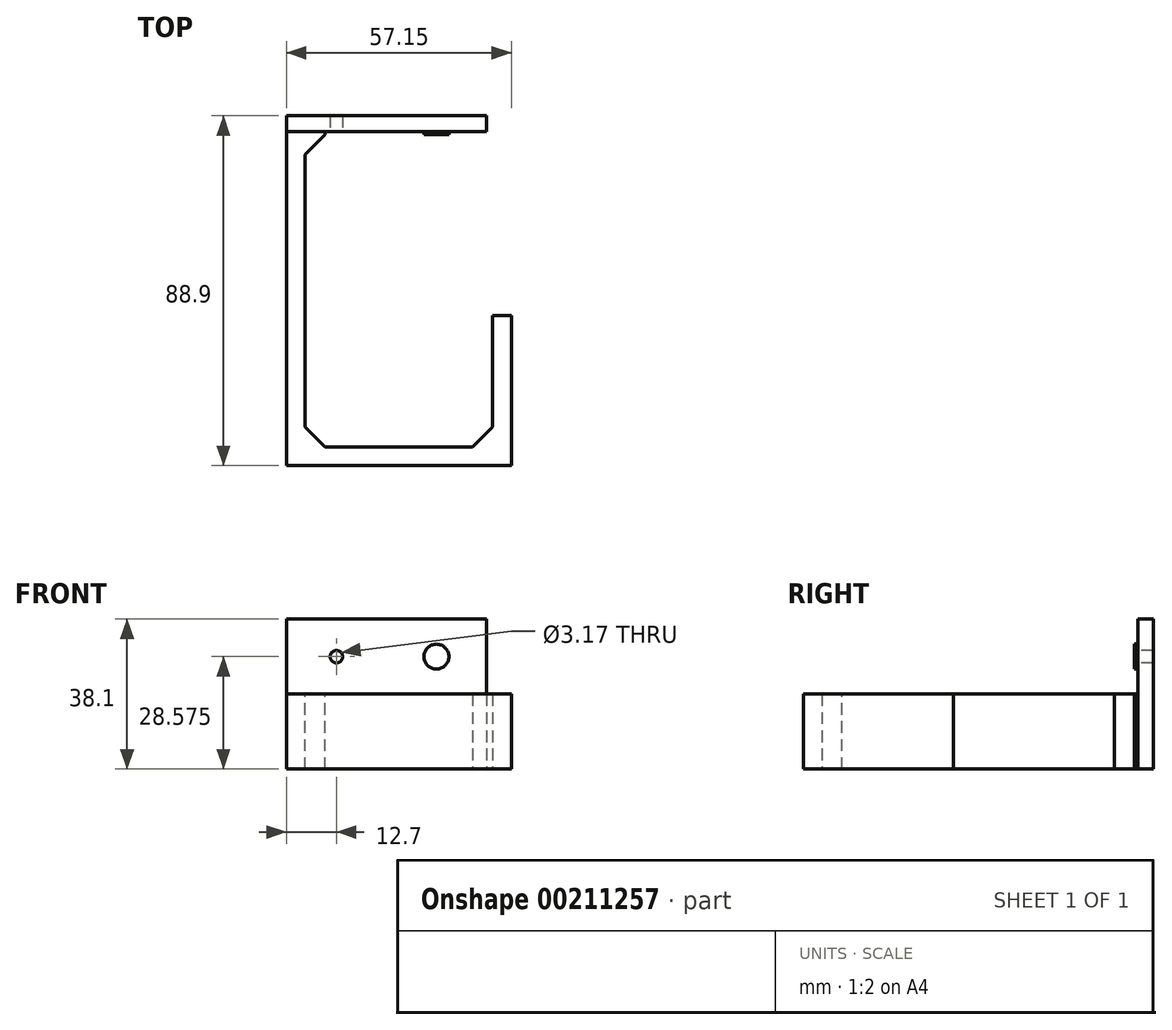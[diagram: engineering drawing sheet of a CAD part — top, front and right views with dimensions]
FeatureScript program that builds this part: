
annotation { "Feature Type Name" : "Feature", "Feature Type Description" : "" }
export const myFeature = defineFeature(function(context is Context, id is Id, definition is map)
    precondition{}
    {
        {
            var Q0;
            Q0=qCreatedBy(makeId("Top.planeOp"),FACE);
            var sketch = newSketch(context, id + "F0", { "sketchPlane" : qUnion([Q0])});
            skLineSegment(sketch, "E0.bottom", {"start": v(-25.4, 25.4) * mm, "end": v(25.4, 25.4) * mm});
            skLineSegment(sketch, "E0.top", {"start": v(-25.4, 30.16) * mm, "end": v(25.4, 30.16) * mm});
            skLineSegment(sketch, "E0.left", {"start": v(-25.4, 25.4) * mm, "end": v(-25.4, 30.16) * mm});
            skLineSegment(sketch, "E0.right", {"start": v(25.4, 25.4) * mm, "end": v(25.4, 30.16) * mm});
            skPoint(sketch, "E0.middle", {"position": v(0, 27.78) * mm});
            skLineSegment(sketch, "E1.bottom", {"start": v(-25.4, 25.4) * mm, "end": v(-20.64, 25.4) * mm});
            skLineSegment(sketch, "E1.top", {"start": v(-25.4, -58.74) * mm, "end": v(-20.64, -58.74) * mm});
            skLineSegment(sketch, "E1.left", {"start": v(-25.4, 25.4) * mm, "end": v(-25.4, -58.74) * mm});
            skLineSegment(sketch, "E1.right", {"start": v(-20.64, 25.4) * mm, "end": v(-20.64, -58.74) * mm});
            skLineSegment(sketch, "E2.bottom", {"start": v(-20.64, -58.74) * mm, "end": v(31.75, -58.74) * mm});
            skLineSegment(sketch, "E2.top", {"start": v(-20.64, -53.98) * mm, "end": v(31.75, -53.98) * mm});
            skLineSegment(sketch, "E2.left", {"start": v(-20.64, -58.74) * mm, "end": v(-20.64, -53.98) * mm});
            skLineSegment(sketch, "E2.right", {"start": v(31.75, -58.74) * mm, "end": v(31.75, -53.97) * mm});
            skLineSegment(sketch, "E3.bottom", {"start": v(31.75, -53.97) * mm, "end": v(26.99, -53.97) * mm});
            skLineSegment(sketch, "E3.top", {"start": v(31.75, -20.64) * mm, "end": v(26.99, -20.64) * mm});
            skLineSegment(sketch, "E3.left", {"start": v(31.75, -53.97) * mm, "end": v(31.75, -20.64) * mm});
            skLineSegment(sketch, "E3.right", {"start": v(26.99, -53.97) * mm, "end": v(26.99, -20.64) * mm});
            skSolve(sketch);
        }
        {
            var Q0;
            Q0 = qSketchRegion(id + "F0", true);
            extrude(context, id + "F1", {"entities" : qUnion([Q0]), "depth" : 19.05 * mm});
        }
        {
            var Q0;
            Q0=makeQuery(id+"F1.opExtrude","SWEPT_EDGE",EDGE,{"disambiguationData":[OSD([sQuery(id+"F0.wireOp",EDGE,"E1.right"),sQuery(id+"F0.wireOp",EDGE,"E2.top"),sQuery(id+"F0.wireOp",EDGE,"E2.left")])]});
            var Q1;
            Q1=makeQuery(id+"F1.opExtrude","SWEPT_EDGE",EDGE,{"disambiguationData":[OSD([sQuery(id+"F0.wireOp",EDGE,"E0.bottom"),sQuery(id+"F0.wireOp",EDGE,"E1.bottom"),sQuery(id+"F0.wireOp",EDGE,"E1.right")])]});
            var Q2;
            Q2=makeQuery(id+"F1.opExtrude","SWEPT_EDGE",EDGE,{"disambiguationData":[OSD([sQuery(id+"F0.wireOp",EDGE,"E2.top"),sQuery(id+"F0.wireOp",EDGE,"E3.bottom"),sQuery(id+"F0.wireOp",EDGE,"E3.right")])]});
            chamfer(context, id + "F2", {"entities" : qUnion([Q0, Q1, Q2]), "width" : 5.08 * mm, "tangentPropagation" : true});
        }
        {
            var Q0;
            Q0=makeQuery(id+"F0.imprint","IMPRINT",FACE,{"disambiguationData":[TD([[makeQuery(id+"F0.imprint","IMPRINT",EDGE,{"derivedFrom":sQuery(id+"F0.wireOp",EDGE,"E0.bottom")}),1.0]])]});
            extrude(context, id + "F3", {"entities" : qUnion([Q0]), "operationType" : NewBodyOperationType.ADD, "depth" : 38.1 * mm});
        }
        {
            var Q0;
            {var subQ0=sQuery(id+"F0.wireOp",EDGE,"E0.bottom");Q0=makeQuery(id+"F3.boolean.opBoolean","MERGE",FACE,{"derivedFrom":[makeQuery(id+"F1.opExtrude","SWEPT_FACE",FACE,{"disambiguationData":[OSD([subQ0])]}),makeQuery(id+"F3.opExtrude","SWEPT_FACE",FACE,{"disambiguationData":[OSD([subQ0,sQuery(id+"F0.wireOp",EDGE,"E1.bottom")])]})]});}
            var sketch = newSketch(context, id + "F4", { "sketchPlane" : qUnion([Q0])});
            skLineSegment(sketch, "E4", {"start": v(-25.4, 28.58) * mm, "end": v(25.4, 28.58) * mm, "construction": true});
            skCircle(sketch, "E5", {"center": v(-12.7, 28.58) * mm, "radius": 3.18 * mm});
            skLineSegment(sketch, "E6", {"start": v(0, 38.1) * mm, "end": v(0, 0) * mm, "construction": true});
            skCircle(sketch, "E7", {"center": v(-12.7, 28.58) * mm, "radius": 1.59 * mm});
            skCircle(sketch, "E8.MirrorC", {"center": v(12.7, 28.58) * mm, "radius": 3.18 * mm});
            skCircle(sketch, "E9.MirrorC", {"center": v(12.7, 28.58) * mm, "radius": 1.59 * mm});
            skSolve(sketch);
        }
        {
            var Q0;
            Q0=makeQuery(id+"F4.imprint","IMPRINT",FACE,{"disambiguationData":[TD([[makeQuery(id+"F4.imprint","IMPRINT",EDGE,{"derivedFrom":sQuery(id+"F4.wireOp",EDGE,"E5")}),1.0]])]});
            var Q1;
            Q1=makeQuery(id+"F4.imprint","IMPRINT",FACE,{"disambiguationData":[TD([[makeQuery(id+"F4.imprint","IMPRINT",EDGE,{"derivedFrom":sQuery(id+"F4.wireOp",EDGE,"E8.MirrorC")}),-1.0]])]});
            extrude(context, id + "F5", {"entities" : qUnion([Q0, Q1]), "operationType" : NewBodyOperationType.REMOVE, "oppositeDirection" : true, "depth" : 0.8 * mm});
        }
        {
            var Q0;
            {var subQ0=sQuery(id+"F0.wireOp",EDGE,"E0.bottom");Q0=makeQuery(id+"F5.boolean.opBoolean","SPLIT",FACE,{"disambiguationData":[TD([makeQuery(id+"F5.opExtrude","SWEPT_FACE",FACE,{"disambiguationData":[OSD([sQuery(id+"F4.wireOp",EDGE,"E7")])]})])],"derivedFrom":makeQuery(id+"F3.boolean.opBoolean","MERGE",FACE,{"derivedFrom":[makeQuery(id+"F1.opExtrude","SWEPT_FACE",FACE,{"disambiguationData":[OSD([subQ0])]}),makeQuery(id+"F3.opExtrude","SWEPT_FACE",FACE,{"disambiguationData":[OSD([subQ0,sQuery(id+"F0.wireOp",EDGE,"E1.bottom")])]})]})});}
            var Q1;
            {var subQ0=sQuery(id+"F0.wireOp",EDGE,"E0.bottom");Q1=makeQuery(id+"F5.boolean.opBoolean","SPLIT",FACE,{"disambiguationData":[TD([makeQuery(id+"F5.opExtrude","SWEPT_FACE",FACE,{"disambiguationData":[OSD([sQuery(id+"F4.wireOp",EDGE,"E9.MirrorC")])]})])],"derivedFrom":makeQuery(id+"F3.boolean.opBoolean","MERGE",FACE,{"derivedFrom":[makeQuery(id+"F1.opExtrude","SWEPT_FACE",FACE,{"disambiguationData":[OSD([subQ0])]}),makeQuery(id+"F3.opExtrude","SWEPT_FACE",FACE,{"disambiguationData":[OSD([subQ0,sQuery(id+"F0.wireOp",EDGE,"E1.bottom")])]})]})});}
            var Q2;
            {var subQ0=sQuery(id+"F0.wireOp",EDGE,"E0.top");Q2=makeQuery(id+"F3.boolean.opBoolean","MERGE",FACE,{"derivedFrom":[makeQuery(id+"F1.opExtrude","SWEPT_FACE",FACE,{"disambiguationData":[OSD([subQ0])]}),makeQuery(id+"F3.opExtrude","SWEPT_FACE",FACE,{"disambiguationData":[OSD([subQ0])]})]});}
            extrude(context, id + "F6", {"entities" : qUnion([Q0, Q1]), "operationType" : NewBodyOperationType.REMOVE, "endBound" : BoundingType.UP_TO_SURFACE, "oppositeDirection" : true, "endBoundEntityFace" : qUnion([Q2]), "depth" : 25.4 * mm});
        }
    });
